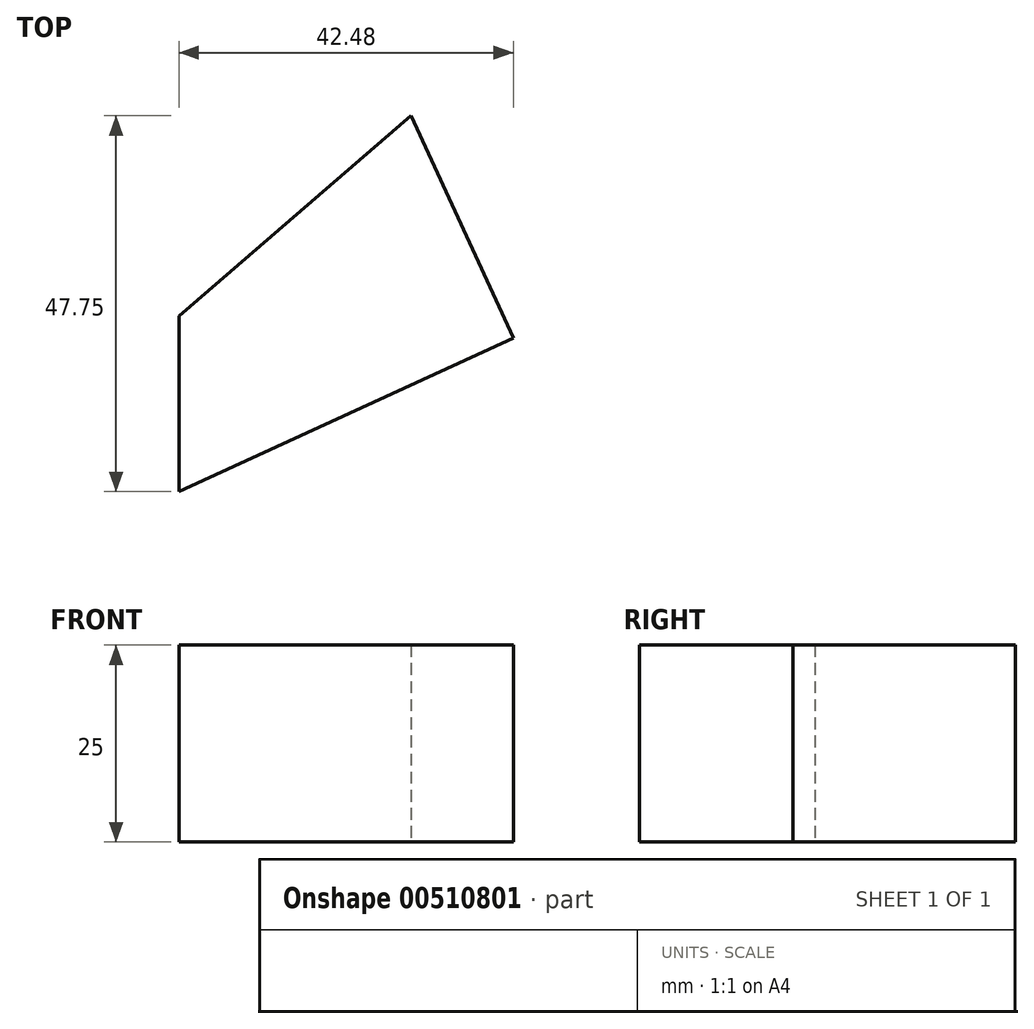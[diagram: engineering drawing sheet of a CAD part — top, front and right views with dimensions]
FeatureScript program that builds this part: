
annotation { "Feature Type Name" : "Feature", "Feature Type Description" : "" }
export const myFeature = defineFeature(function(context is Context, id is Id, definition is map)
    precondition{}
    {
        {
            var Q0;
            Q0=qCreatedBy(makeId("Top.planeOp"),FACE);
            var sketch = newSketch(context, id + "F0", { "sketchPlane" : qUnion([Q0])});
            skLineSegment(sketch, "E0", {"start": v(0, 22.3) * mm, "end": v(0, 0) * mm});
            skLineSegment(sketch, "E1", {"start": v(0, 0) * mm, "end": v(42.48, 19.52) * mm});
            skLineSegment(sketch, "E2", {"start": v(42.48, 19.52) * mm, "end": v(29.5, 47.75) * mm});
            skLineSegment(sketch, "E3", {"start": v(29.5, 47.75) * mm, "end": v(0, 22.3) * mm});
            skSolve(sketch);
        }
        {
            var Q0;
            Q0 = qSketchRegion(id + "F0", true);
            extrude(context, id + "F1", {"entities" : qUnion([Q0]), "depth" : 25 * mm});
        }
    });
